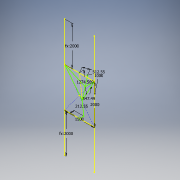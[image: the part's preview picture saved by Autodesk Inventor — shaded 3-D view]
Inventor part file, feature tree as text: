
AUTODESK INVENTOR PART (.ipt)
format: ipt  version: 2018 (Build 220112000, 112)  size: 104,448 bytes
history: native  units: mm
features: sketch x2
ambient origin geometry x8: Origin, YZ Plane, XZ Plane, XY Plane, X Axis, Y Axis, Z Axis, Center Point
feature tree (2):
  sketch  "Sketch1"  dims[d0=1500.0mm d1=2000.0mm d2=2000.0mm d4=2000.0mm d5=1274.568697mm d6=212.55mm d7=512.55mm d8=547.49mm d10=1000.0mm]
  sketch  "3D Sketch2"
